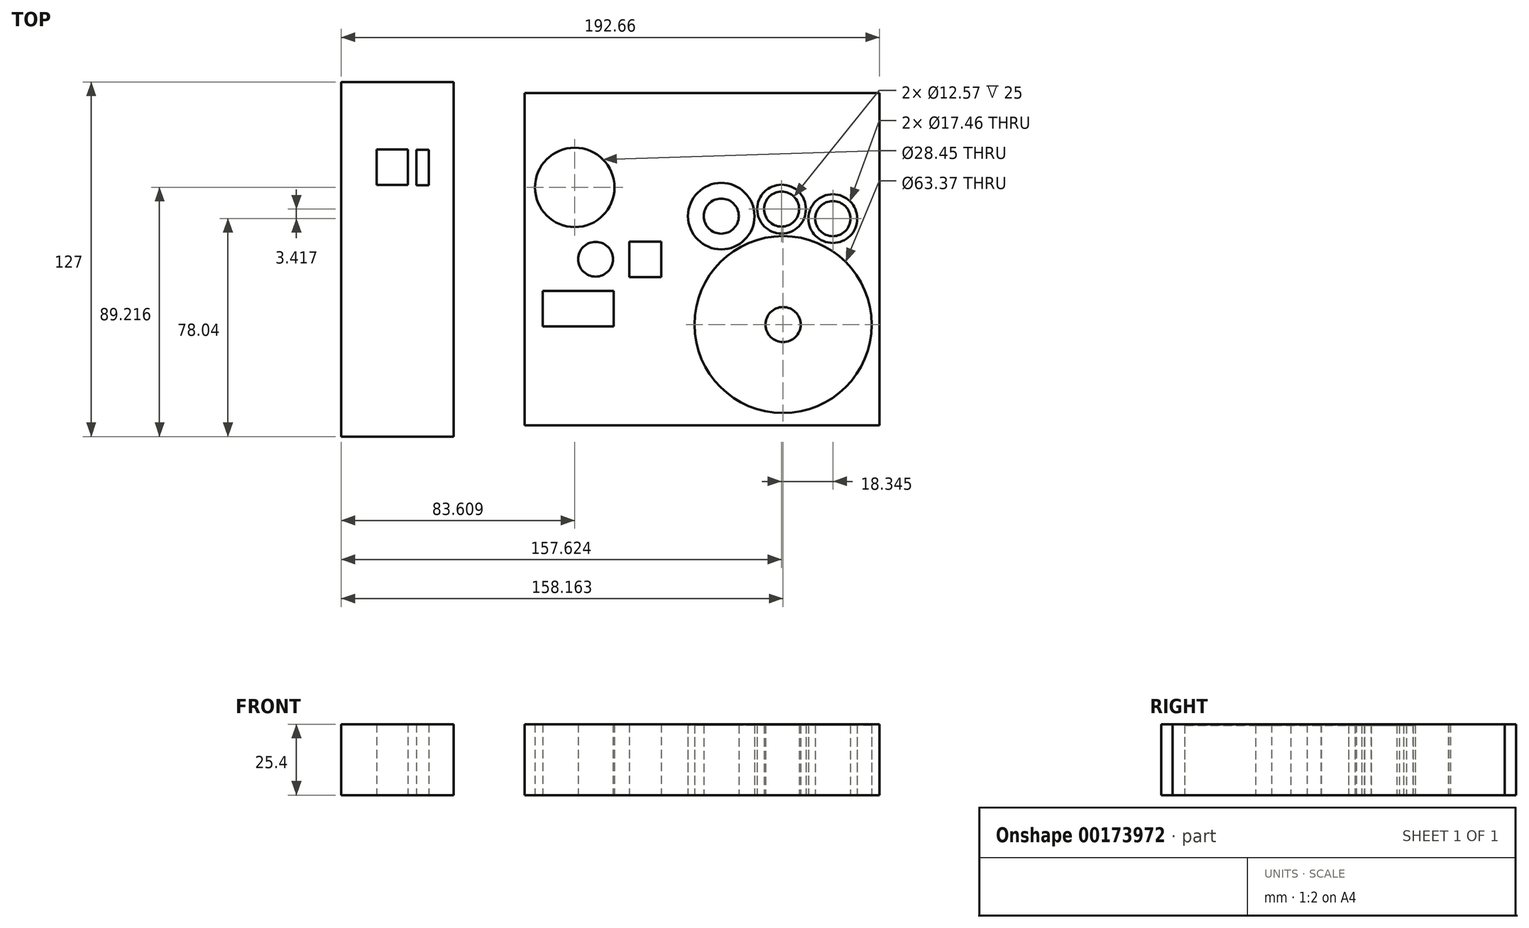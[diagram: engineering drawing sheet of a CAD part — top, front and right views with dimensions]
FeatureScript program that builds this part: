
annotation { "Feature Type Name" : "Feature", "Feature Type Description" : "" }
export const myFeature = defineFeature(function(context is Context, id is Id, definition is map)
    precondition{}
    {
        {
            var Q0;
            Q0=qCreatedBy(makeId("Top.planeOp"),FACE);
            var sketch = newSketch(context, id + "F0", { "sketchPlane" : qUnion([Q0])});
            skLineSegment(sketch, "E0", {"start": v(0, 0) * mm, "end": v(76.2, 0) * mm, "construction": true});
            skLineSegment(sketch, "E1.bottom", {"start": v(-12.7, -63.5) * mm, "end": v(-52.96, -63.5) * mm});
            skLineSegment(sketch, "E1.top", {"start": v(-12.7, 63.5) * mm, "end": v(-52.96, 63.5) * mm});
            skLineSegment(sketch, "E1.left", {"start": v(-12.7, -63.5) * mm, "end": v(-12.7, 63.5) * mm});
            skLineSegment(sketch, "E1.right", {"start": v(-52.96, -63.5) * mm, "end": v(-52.96, 63.5) * mm});
            skLineSegment(sketch, "E2.bottom", {"start": v(12.7, 59.46) * mm, "end": v(139.7, 59.46) * mm});
            skLineSegment(sketch, "E2.top", {"start": v(12.7, -59.46) * mm, "end": v(139.7, -59.46) * mm});
            skLineSegment(sketch, "E2.left", {"start": v(12.7, 59.46) * mm, "end": v(12.7, -59.46) * mm});
            skLineSegment(sketch, "E2.right", {"start": v(139.7, 59.46) * mm, "end": v(139.7, -59.46) * mm});
            skPoint(sketch, "E2.middle", {"position": v(76.2, 0) * mm});
            skCircle(sketch, "E3", {"center": v(38.1, 0) * mm, "radius": 6.22 * mm});
            skCircle(sketch, "E4", {"center": v(30.65, 25.72) * mm, "radius": 14.22 * mm});
            skLineSegment(sketch, "E5.bottom", {"start": v(61.6, -6.35) * mm, "end": v(50.16, -6.35) * mm});
            skLineSegment(sketch, "E5.top", {"start": v(61.6, 6.35) * mm, "end": v(50.16, 6.35) * mm});
            skLineSegment(sketch, "E5.left", {"start": v(61.6, -6.35) * mm, "end": v(61.6, 6.35) * mm});
            skLineSegment(sketch, "E5.right", {"start": v(50.16, -6.35) * mm, "end": v(50.16, 6.35) * mm});
            skPoint(sketch, "E5.middle", {"position": v(55.88, 0) * mm});
            skLineSegment(sketch, "E6.bottom", {"start": v(44.55, -11.3) * mm, "end": v(19.15, -11.3) * mm});
            skLineSegment(sketch, "E6.top", {"start": v(44.55, -24) * mm, "end": v(19.15, -24) * mm});
            skLineSegment(sketch, "E6.left", {"start": v(44.55, -11.3) * mm, "end": v(44.55, -24) * mm});
            skLineSegment(sketch, "E6.right", {"start": v(19.15, -11.3) * mm, "end": v(19.15, -24) * mm});
            skLineSegment(sketch, "E7.bottom", {"start": v(-40.26, 39.37) * mm, "end": v(-29.08, 39.37) * mm});
            skLineSegment(sketch, "E7.top", {"start": v(-40.26, 26.67) * mm, "end": v(-29.08, 26.67) * mm});
            skLineSegment(sketch, "E7.left", {"start": v(-40.26, 39.37) * mm, "end": v(-40.26, 26.67) * mm});
            skLineSegment(sketch, "E7.right", {"start": v(-29.08, 39.37) * mm, "end": v(-29.08, 26.67) * mm});
            skLineSegment(sketch, "E8.bottom", {"start": v(-25.99, 39.22) * mm, "end": v(-21.6, 39.22) * mm});
            skLineSegment(sketch, "E8.top", {"start": v(-25.99, 26.52) * mm, "end": v(-21.6, 26.52) * mm});
            skLineSegment(sketch, "E8.left", {"start": v(-25.99, 39.22) * mm, "end": v(-25.99, 26.52) * mm});
            skLineSegment(sketch, "E8.right", {"start": v(-21.6, 39.22) * mm, "end": v(-21.6, 26.52) * mm});
            skCircle(sketch, "E9", {"center": v(104.66, 17.96) * mm, "radius": 6.29 * mm});
            skCircle(sketch, "E10", {"center": v(104.66, 17.96) * mm, "radius": 8.73 * mm});
            skCircle(sketch, "E11", {"center": v(83.08, 15.44) * mm, "radius": 6.29 * mm});
            skCircle(sketch, "E12", {"center": v(83.08, 15.44) * mm, "radius": 11.9 * mm});
            skCircle(sketch, "E13", {"center": v(105.2, -23.4) * mm, "radius": 6.29 * mm});
            skCircle(sketch, "E14", {"center": v(105.2, -23.4) * mm, "radius": 31.69 * mm});
            skCircle(sketch, "E15", {"center": v(123, 14.54) * mm, "radius": 6.29 * mm});
            skCircle(sketch, "E16", {"center": v(123, 14.54) * mm, "radius": 8.73 * mm});
            skSolve(sketch);
        }
        {
            var Q0;
            Q0 = qSketchRegion(id + "F0", true);
            extrude(context, id + "F1", {"entities" : qUnion([Q0]), "depth" : 25.4 * mm});
        }
        {
            var Q0;
            Q0=makeQuery(id+"F0.imprint","IMPRINT",FACE,{"disambiguationData":[TD([[makeQuery(id+"F0.imprint","IMPRINT",EDGE,{"derivedFrom":sQuery(id+"F0.wireOp",EDGE,"E13")}),-1.0]])]});
            var Q1;
            Q1=makeQuery(id+"F0.imprint","IMPRINT",FACE,{"disambiguationData":[TD([[makeQuery(id+"F0.imprint","IMPRINT",EDGE,{"derivedFrom":sQuery(id+"F0.wireOp",EDGE,"E11")}),-1.0]])]});
            var Q2;
            Q2=makeQuery(id+"F0.imprint","IMPRINT",FACE,{"disambiguationData":[TD([[makeQuery(id+"F0.imprint","IMPRINT",EDGE,{"derivedFrom":sQuery(id+"F0.wireOp",EDGE,"E9")}),-1.0]])]});
            var Q3;
            Q3=makeQuery(id+"F0.imprint","IMPRINT",FACE,{"disambiguationData":[TD([[makeQuery(id+"F0.imprint","IMPRINT",EDGE,{"derivedFrom":sQuery(id+"F0.wireOp",EDGE,"E15")}),-1.0]])]});
            extrude(context, id + "F2", {"entities" : qUnion([Q0, Q1, Q2, Q3]), "depth" : 25 * mm});
        }
    });
